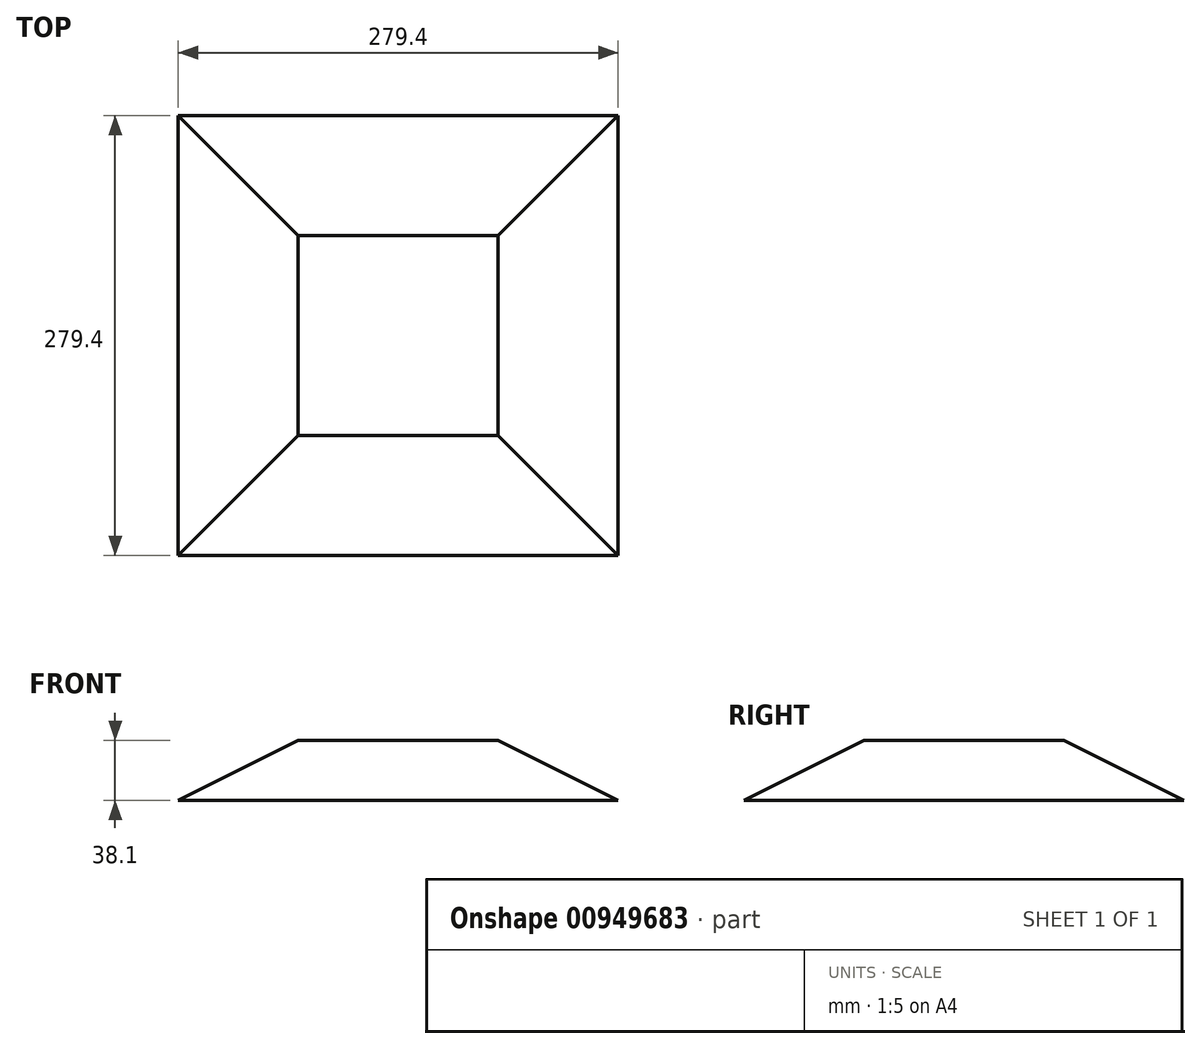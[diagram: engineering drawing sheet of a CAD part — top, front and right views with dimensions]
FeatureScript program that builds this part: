
annotation { "Feature Type Name" : "Feature", "Feature Type Description" : "" }
export const myFeature = defineFeature(function(context is Context, id is Id, definition is map)
    precondition{}
    {
        {
            var Q0;
            Q0=qCreatedBy(makeId("Front.planeOp"),FACE);
            var sketch = newSketch(context, id + "F0", { "sketchPlane" : qUnion([Q0])});
            skLineSegment(sketch, "E0", {"start": v(-139.7, -38.1) * mm, "end": v(139.7, -38.1) * mm});
            skLineSegment(sketch, "E1", {"start": v(0, 0) * mm, "end": v(0, -38.1) * mm});
            skLineSegment(sketch, "E2", {"start": v(-63.5, 0) * mm, "end": v(63.5, 0) * mm});
            skLineSegment(sketch, "E3", {"start": v(-63.5, 0) * mm, "end": v(-139.7, -38.1) * mm});
            skLineSegment(sketch, "E4", {"start": v(63.5, 0) * mm, "end": v(139.7, -38.1) * mm});
            skLineSegment(sketch, "E5", {"start": v(-63.5, 0) * mm, "end": v(-63.5, -38.1) * mm});
            skSolve(sketch);
        }
        {
            var Q0;
            {var subQ0=sQuery(id+"F0.wireOp",EDGE,"E1");Q0=makeQuery(id+"F0.imprint","IMPRINT",FACE,{"disambiguationData":[TD([[makeQuery(id+"F0.imprint","IMPRINT",EDGE,{"derivedFrom":subQ0}),-1.0]])]});}
            var Q1;
            {var subQ2=sQuery(id+"F0.wireOp",EDGE,"E1");Q1=makeQuery(id+"F0.imprint","IMPRINT",FACE,{"disambiguationData":[TD([[makeQuery(id+"F0.imprint","IMPRINT",EDGE,{"derivedFrom":subQ2}),1.0]])]});}
            var Q2;
            {var subQ0=sQuery(id+"F0.wireOp",EDGE,"E3");Q2=makeQuery(id+"F0.imprint","IMPRINT",FACE,{"disambiguationData":[TD([[makeQuery(id+"F0.imprint","IMPRINT",EDGE,{"derivedFrom":subQ0}),1.0]])]});}
            extrude(context, id + "F1", {"entities" : qUnion([Q0, Q1, Q2]), "depth" : 279.4 * mm, "offsetDistance" : 25.4 * mm});
        }
        {
            var Q0;
            Q0=makeQuery(id+"F1.opExtrude","CAP_EDGE",EDGE,{"disambiguationData":[OSD([sQuery(id+"F0.wireOp",EDGE,"E2")])],"isStart":false});
            var Q1;
            Q1=makeQuery(id+"F1.opExtrude","CAP_EDGE",EDGE,{"disambiguationData":[OSD([sQuery(id+"F0.wireOp",EDGE,"E2")])],"isStart":true});
            chamfer(context, id + "F2", {"entities" : qUnion([Q0, Q1]), "chamferType" : ChamferType.TWO_OFFSETS, "width1" : 38.1 * mm, "oppositeDirection" : true, "width2" : 76.2 * mm, "tangentPropagation" : true});
        }
    });
